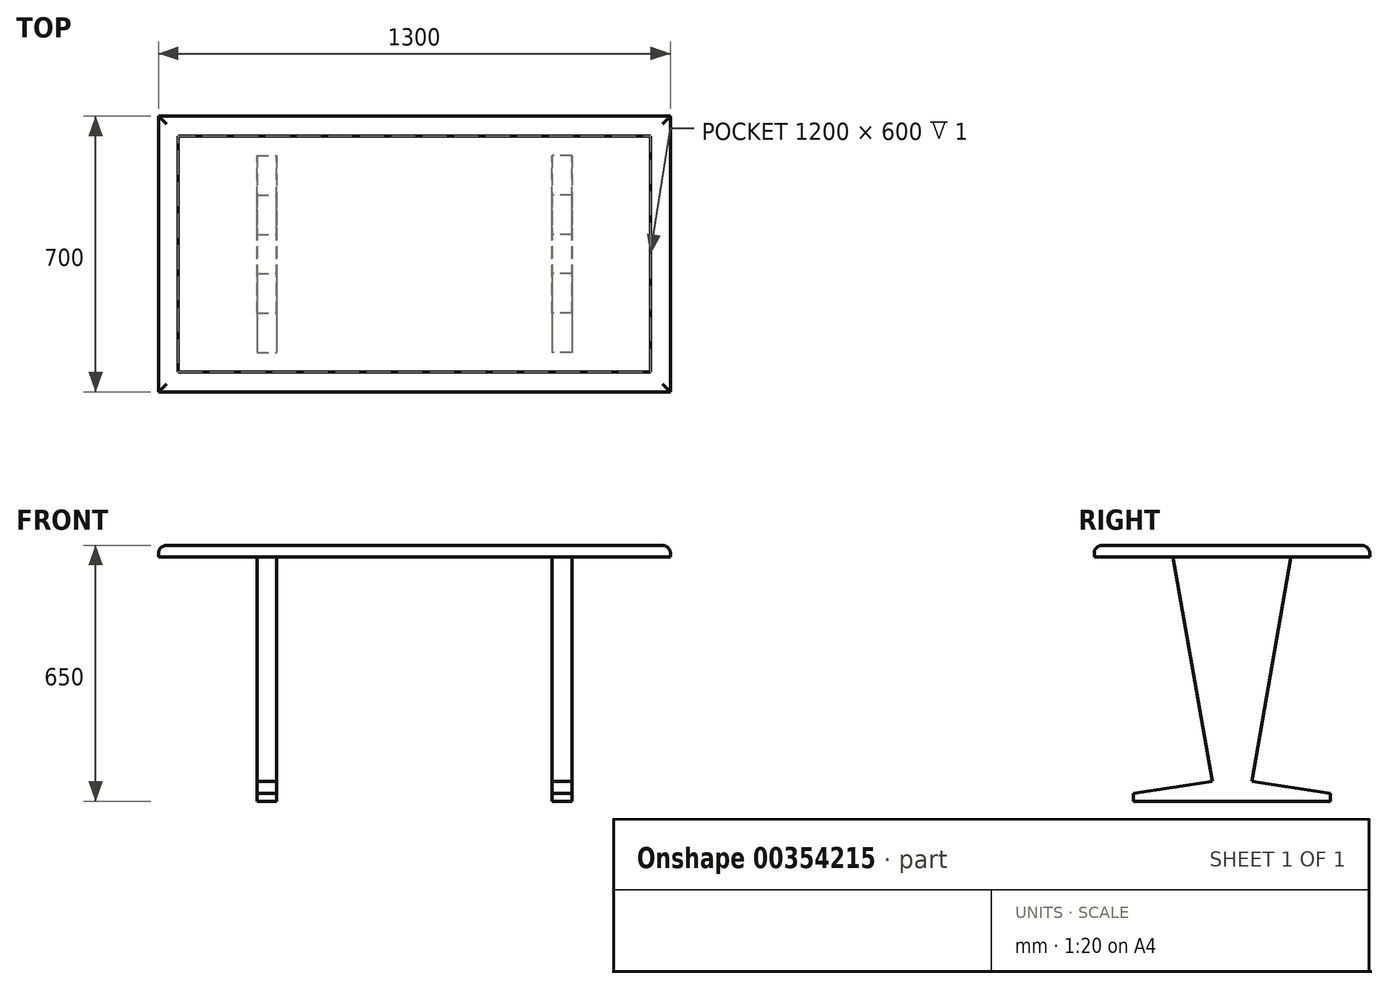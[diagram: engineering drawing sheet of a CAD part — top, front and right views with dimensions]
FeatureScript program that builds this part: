
annotation { "Feature Type Name" : "Feature", "Feature Type Description" : "" }
export const myFeature = defineFeature(function(context is Context, id is Id, definition is map)
    precondition{}
    {
        {
            var Q0;
            Q0=qCreatedBy(makeId("Top.planeOp"),FACE);
            var sketch = newSketch(context, id + "F0", { "sketchPlane" : qUnion([Q0])});
            skLineSegment(sketch, "E0.bottom", {"start": v(0, 350) * mm, "end": v(650, 350) * mm});
            skLineSegment(sketch, "E0.top", {"start": v(0, -350) * mm, "end": v(650, -350) * mm});
            skLineSegment(sketch, "E0.left", {"start": v(0, 350) * mm, "end": v(0, -350) * mm});
            skLineSegment(sketch, "E0.right", {"start": v(650, 350) * mm, "end": v(650, -350) * mm});
            skSolve(sketch);
        }
        {
            var Q0;
            Q0=makeQuery(id+"F0.imprint","IMPRINT",FACE,{"disambiguationData":[TD([[makeQuery(id+"F0.imprint","IMPRINT",EDGE,{"derivedFrom":sQuery(id+"F0.wireOp",EDGE,"E0.bottom")}),-1.0]])]});
            extrude(context, id + "F1", {"entities" : qUnion([Q0]), "oppositeDirection" : true, "depth" : 30 * mm});
        }
        {
            var Q0;
            Q0=qCreatedBy(makeId("Right.planeOp"),FACE);
            var sketch = newSketch(context, id + "F2", { "sketchPlane" : qUnion([Q0])});
            skLineSegment(sketch, "E1", {"start": v(0, -30) * mm, "end": v(-150, -30) * mm});
            skLineSegment(sketch, "E2", {"start": v(-150, -30) * mm, "end": v(-50, -600) * mm});
            skLineSegment(sketch, "E3", {"start": v(-50, -600) * mm, "end": v(-250, -630) * mm});
            skLineSegment(sketch, "E4", {"start": v(-250, -630) * mm, "end": v(-250, -650) * mm});
            skLineSegment(sketch, "E5", {"start": v(-250, -650) * mm, "end": v(0, -650) * mm});
            skLineSegment(sketch, "E6", {"start": v(0, -650) * mm, "end": v(0, -30) * mm});
            skLineSegment(sketch, "E7.MirrorCS", {"start": v(0, -30) * mm, "end": v(150, -30) * mm});
            skLineSegment(sketch, "E8.MirrorCS", {"start": v(150, -30) * mm, "end": v(50, -600) * mm});
            skLineSegment(sketch, "E9.MirrorCS", {"start": v(50, -600) * mm, "end": v(250, -630) * mm});
            skLineSegment(sketch, "E10.MirrorCS", {"start": v(250, -630) * mm, "end": v(250, -650) * mm});
            skLineSegment(sketch, "E11.MirrorCS", {"start": v(250, -650) * mm, "end": v(0, -650) * mm});
            skSolve(sketch);
        }
        {
            var Q0;
            Q0=makeQuery(id+"F2.imprint","IMPRINT",FACE,{"disambiguationData":[TD([[makeQuery(id+"F2.imprint","IMPRINT",EDGE,{"derivedFrom":sQuery(id+"F2.wireOp",EDGE,"E6")}),-1.0]])]});
            var Q1;
            Q1=makeQuery(id+"F2.imprint","IMPRINT",FACE,{"disambiguationData":[TD([[makeQuery(id+"F2.imprint","IMPRINT",EDGE,{"derivedFrom":sQuery(id+"F2.wireOp",EDGE,"E1")}),1.0]])]});
            extrude(context, id + "F3", {"entities" : qUnion([Q0, Q1]), "operationType" : NewBodyOperationType.ADD, "depth" : 400 * mm, "hasSecondDirection" : true, "secondDirectionOppositeDirection" : false, "secondDirectionDepth" : 350 * mm});
        }
        {
            var Q0;
            Q0=makeQuery(id+"F1.opExtrude","SWEPT_BODY",BODY,{"disambiguationData":[OSD([sQuery(id+"F0.wireOp",EDGE,"E0.bottom"),sQuery(id+"F0.wireOp",EDGE,"E0.top"),sQuery(id+"F0.wireOp",EDGE,"E0.left"),sQuery(id+"F0.wireOp",EDGE,"E0.right")])]});
            var Q1;
            Q1=qCreatedBy(makeId("Right.planeOp"),FACE);
            mirror(context, id + "F4", {"operationType" : NewBodyOperationType.ADD, "entities" : qUnion([Q0]), "mirrorPlane" : qUnion([Q1])});
        }
        {
            var Q0;
            {var subQ0=makeQuery(id+"F1.opExtrude","CAP_FACE",FACE,{"disambiguationData":[OSD([sQuery(id+"F0.wireOp",EDGE,"E0.bottom"),sQuery(id+"F0.wireOp",EDGE,"E0.top"),sQuery(id+"F0.wireOp",EDGE,"E0.left"),sQuery(id+"F0.wireOp",EDGE,"E0.right")])],"isStart":true});Q0=makeQuery(id+"F4.boolean.opBoolean","MERGE",FACE,{"derivedFrom":[subQ0,makeQuery(id+"F4.opPattern","COPY",FACE,{"derivedFrom":subQ0,"instanceName":"1"})]});}
            fillet(context, id + "F5", {"entities" : qUnion([Q0]), "radius" : 20 * mm, "tangentPropagation" : true, "allowEdgeOverflow" : false});
        }
        {
            var Q0;
            Q0=qCreatedBy(makeId("Top.planeOp"),FACE);
            var sketch = newSketch(context, id + "F6", { "sketchPlane" : qUnion([Q0])});
            skLineSegment(sketch, "E12.bottom", {"start": v(-600, 300) * mm, "end": v(600, 300) * mm});
            skLineSegment(sketch, "E12.top", {"start": v(-600, -300) * mm, "end": v(600, -300) * mm});
            skLineSegment(sketch, "E12.left", {"start": v(-600, 300) * mm, "end": v(-600, -300) * mm});
            skLineSegment(sketch, "E12.right", {"start": v(600, 300) * mm, "end": v(600, -300) * mm});
            skSolve(sketch);
        }
        {
            var Q0;
            Q0=makeQuery(id+"F6.imprint","IMPRINT",FACE,{"disambiguationData":[TD([[makeQuery(id+"F6.imprint","IMPRINT",EDGE,{"derivedFrom":sQuery(id+"F6.wireOp",EDGE,"E12.bottom")}),-1.0]])]});
            extrude(context, id + "F7", {"entities" : qUnion([Q0]), "operationType" : NewBodyOperationType.REMOVE, "oppositeDirection" : true, "depth" : 1 * mm});
        }
    });
